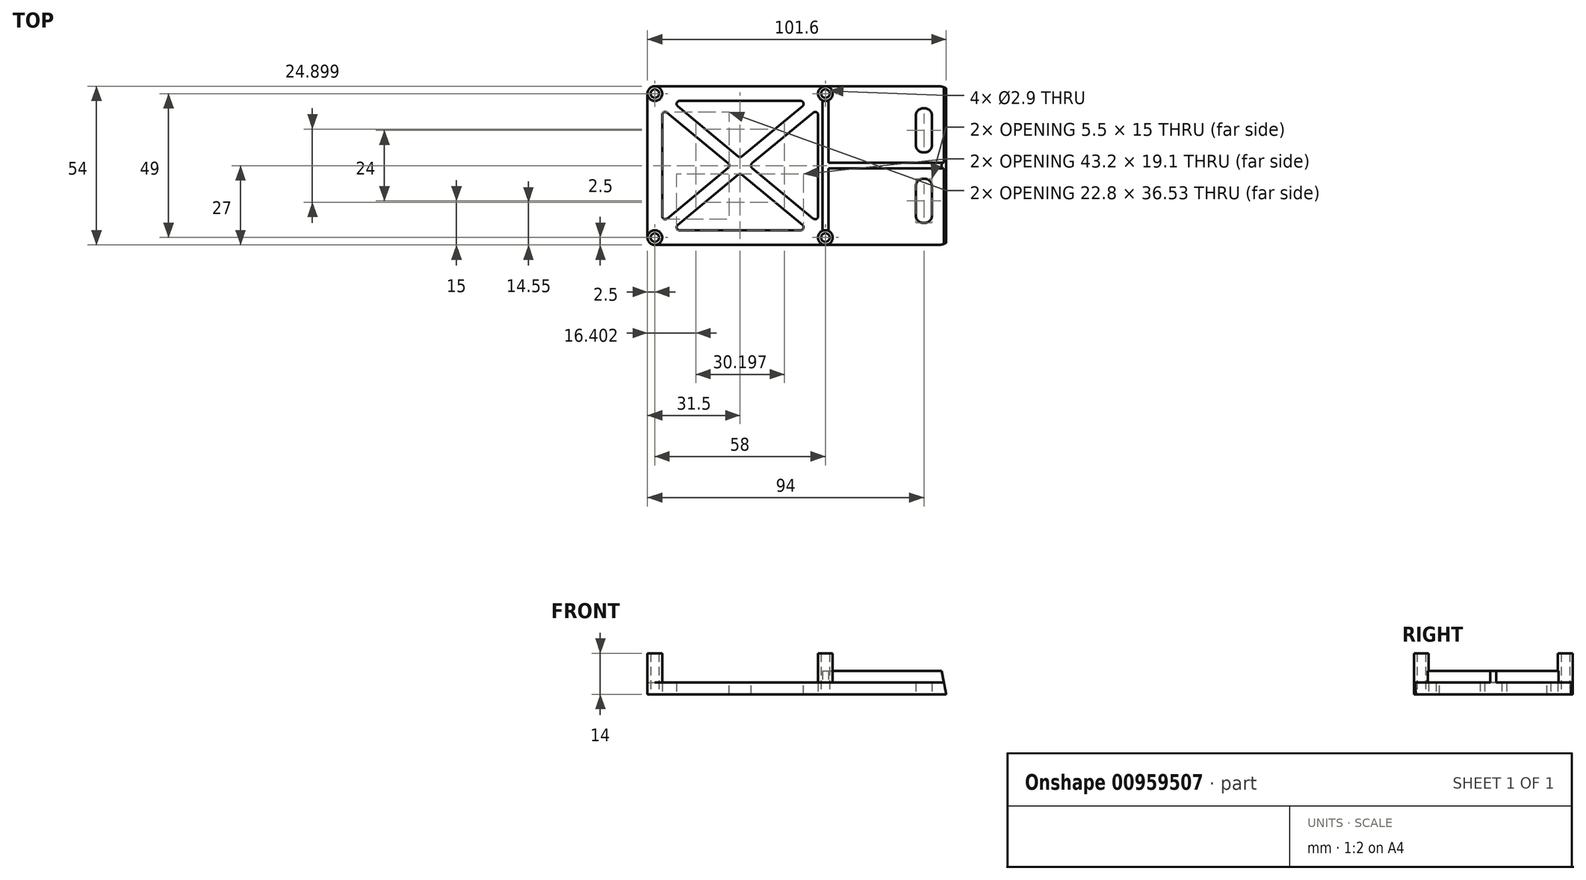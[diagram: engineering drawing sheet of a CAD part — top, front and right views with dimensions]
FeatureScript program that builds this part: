
annotation { "Feature Type Name" : "Feature", "Feature Type Description" : "" }
export const myFeature = defineFeature(function(context is Context, id is Id, definition is map)
    precondition{}
    {
        {
            var Q0;
            Q0=qCreatedBy(makeId("Top.planeOp"),FACE);
            var sketch = newSketch(context, id + "F0", { "sketchPlane" : qUnion([Q0])});
            skLineSegment(sketch, "E0.bottom", {"start": v(37.5, -28) * mm, "end": v(-47.5, -28) * mm, "construction": true});
            skLineSegment(sketch, "E0.top", {"start": v(37.5, 28) * mm, "end": v(-47.5, 28) * mm, "construction": true});
            skLineSegment(sketch, "E0.left", {"start": v(37.5, -28) * mm, "end": v(37.5, 28) * mm, "construction": true});
            skLineSegment(sketch, "E0.right", {"start": v(-47.5, -28) * mm, "end": v(-47.5, 28) * mm, "construction": true});
            skLineSegment(sketch, "E1.bottom", {"start": v(-44, -24.5) * mm, "end": v(14, -24.5) * mm, "construction": true});
            skLineSegment(sketch, "E1.top", {"start": v(-44, 24.5) * mm, "end": v(14, 24.5) * mm, "construction": true});
            skLineSegment(sketch, "E1.left", {"start": v(-44, -24.5) * mm, "end": v(-44, 24.5) * mm, "construction": true});
            skLineSegment(sketch, "E1.right", {"start": v(14, -24.5) * mm, "end": v(14, 24.5) * mm, "construction": true});
            skSolve(sketch);
        }
        {
            var Q0;
            Q0=qCreatedBy(makeId("Top.planeOp"),FACE);
            var sketch = newSketch(context, id + "F1", { "sketchPlane" : qUnion([Q0])});
            skPoint(sketch, "E2.0", {"position": v(-44, 24.5) * mm});
            skPoint(sketch, "E3.0", {"position": v(14, 24.5) * mm});
            skPoint(sketch, "E4.0", {"position": v(14, -24.5) * mm});
            skPoint(sketch, "E5.0", {"position": v(-44, -24.5) * mm});
            skCircle(sketch, "E6", {"center": v(-44, 24.5) * mm, "radius": 2.5 * mm});
            skCircle(sketch, "E7", {"center": v(14, 24.5) * mm, "radius": 2.5 * mm});
            skCircle(sketch, "E8", {"center": v(14, -24.5) * mm, "radius": 2.5 * mm});
            skCircle(sketch, "E9", {"center": v(-44, -24.5) * mm, "radius": 2.5 * mm});
            skCircle(sketch, "E10", {"center": v(-44, 24.5) * mm, "radius": 1.45 * mm});
            skCircle(sketch, "E11", {"center": v(14, 24.5) * mm, "radius": 1.45 * mm});
            skCircle(sketch, "E12", {"center": v(14, -24.5) * mm, "radius": 1.45 * mm});
            skCircle(sketch, "E13", {"center": v(-44, -24.5) * mm, "radius": 1.45 * mm});
            skPoint(sketch, "E14.0", {"position": v(-15, 24.5) * mm});
            skPoint(sketch, "E15.0", {"position": v(-44, 0) * mm});
            skLineSegment(sketch, "E16.bottom", {"start": v(16.5, -27) * mm, "end": v(-46.5, -27) * mm});
            skLineSegment(sketch, "E16.top", {"start": v(16.5, 27) * mm, "end": v(-46.5, 27) * mm});
            skLineSegment(sketch, "E16.left", {"start": v(16.5, -27) * mm, "end": v(16.5, 27) * mm, "construction": true});
            skLineSegment(sketch, "E16.right", {"start": v(-46.5, -27) * mm, "end": v(-46.5, 27) * mm});
            skPoint(sketch, "E16.middle", {"position": v(-15, 0) * mm});
            skLineSegment(sketch, "E17", {"start": v(16.5, -27) * mm, "end": v(57.5, -27) * mm});
            skLineSegment(sketch, "E18", {"start": v(57.5, -27) * mm, "end": v(57.5, 27) * mm});
            skLineSegment(sketch, "E19", {"start": v(57.5, 27) * mm, "end": v(16.5, 27) * mm});
            skLineSegment(sketch, "E20", {"start": v(47.5, 27) * mm, "end": v(47.5, -27) * mm, "construction": true});
            skLineSegment(sketch, "E21.bottom", {"start": v(11.5, -22) * mm, "end": v(-41.5, -22) * mm});
            skLineSegment(sketch, "E21.top", {"start": v(11.5, 22) * mm, "end": v(-41.5, 22) * mm});
            skLineSegment(sketch, "E21.left", {"start": v(11.5, -22) * mm, "end": v(11.5, 22) * mm});
            skLineSegment(sketch, "E21.right", {"start": v(-41.5, -22) * mm, "end": v(-41.5, 22) * mm});
            skLineSegment(sketch, "E22.bottom", {"start": v(50.25, 4.5) * mm, "end": v(44.75, 4.5) * mm});
            skLineSegment(sketch, "E22.top", {"start": v(50.25, 19.5) * mm, "end": v(44.75, 19.5) * mm});
            skLineSegment(sketch, "E22.left", {"start": v(50.25, 4.5) * mm, "end": v(50.25, 19.5) * mm});
            skLineSegment(sketch, "E22.right", {"start": v(44.75, 4.5) * mm, "end": v(44.75, 19.5) * mm});
            skPoint(sketch, "E22.middle", {"position": v(47.5, 12) * mm});
            skLineSegment(sketch, "E23.bottom", {"start": v(44.75, -19.5) * mm, "end": v(50.25, -19.5) * mm});
            skLineSegment(sketch, "E23.top", {"start": v(44.75, -4.5) * mm, "end": v(50.25, -4.5) * mm});
            skLineSegment(sketch, "E23.left", {"start": v(44.75, -19.5) * mm, "end": v(44.75, -4.5) * mm});
            skLineSegment(sketch, "E23.right", {"start": v(50.25, -19.5) * mm, "end": v(50.25, -4.5) * mm});
            skPoint(sketch, "E23.middle", {"position": v(47.5, -12) * mm});
            skPoint(sketch, "E24.0", {"position": v(37.5, 0) * mm});
            skLineSegment(sketch, "E25", {"start": v(11.5, 22) * mm, "end": v(-41.5, -22) * mm, "construction": true});
            skLineSegment(sketch, "E26", {"start": v(-41.5, 22) * mm, "end": v(11.5, -22) * mm, "construction": true});
            skArc(sketch, "E27.0.startCap", {"start": v(-42.78, 20.46) * mm, "mid": v(-43.04, 23.28) * mm, "end": v(-40.22, 23.54) * mm, "construction": true});
            skArc(sketch, "E27.0.endCap", {"start": v(12.78, -20.46) * mm, "mid": v(13.04, -23.28) * mm, "end": v(10.22, -23.54) * mm, "construction": true});
            skLineSegment(sketch, "E27.0.left", {"start": v(-40.22, 23.54) * mm, "end": v(12.78, -20.46) * mm});
            skLineSegment(sketch, "E27.0.right", {"start": v(-42.78, 20.46) * mm, "end": v(10.22, -23.54) * mm});
            skArc(sketch, "E27.1.startCap", {"start": v(10.22, 23.54) * mm, "mid": v(13.04, 23.28) * mm, "end": v(12.78, 20.46) * mm, "construction": true});
            skArc(sketch, "E27.1.endCap", {"start": v(-40.22, -23.54) * mm, "mid": v(-43.04, -23.28) * mm, "end": v(-42.78, -20.46) * mm, "construction": true});
            skLineSegment(sketch, "E27.1.left", {"start": v(12.78, 20.46) * mm, "end": v(-40.22, -23.54) * mm});
            skLineSegment(sketch, "E27.1.right", {"start": v(10.22, 23.54) * mm, "end": v(-42.78, -20.46) * mm});
            skSolve(sketch);
        }
        {
            var Q0;
            Q0=makeQuery(id+"F1.imprint","IMPRINT",FACE,{"disambiguationData":[TD([[makeQuery(id+"F1.imprint","IMPRINT",EDGE,{"derivedFrom":sQuery(id+"F1.wireOp",EDGE,"E7")}),1.0]])]});
            var Q1;
            Q1=makeQuery(id+"F1.imprint","IMPRINT",FACE,{"disambiguationData":[TD([[makeQuery(id+"F1.imprint","IMPRINT",EDGE,{"derivedFrom":sQuery(id+"F1.wireOp",EDGE,"E8")}),1.0]])]});
            var Q2;
            Q2=makeQuery(id+"F1.imprint","IMPRINT",FACE,{"disambiguationData":[TD([[makeQuery(id+"F1.imprint","IMPRINT",EDGE,{"derivedFrom":sQuery(id+"F1.wireOp",EDGE,"E10")}),-1.0]])]});
            var Q3;
            Q3=makeQuery(id+"F1.imprint","IMPRINT",FACE,{"disambiguationData":[TD([[makeQuery(id+"F1.imprint","IMPRINT",EDGE,{"derivedFrom":sQuery(id+"F1.wireOp",EDGE,"E13")}),-1.0]])]});
            var Q4;
            {var subQ13=sQuery(id+"F1.wireOp",EDGE,"E7");Q4=makeQuery(id+"F1.imprint","IMPRINT",FACE,{"disambiguationData":[TD([[makeQuery(id+"F1.imprint","IMPRINT",EDGE,{"derivedFrom":subQ13}),-1.0]])]});}
            var Q5;
            {var subQ1=sQuery(id+"F1.wireOp",EDGE,"E21.right");var subQ5=sQuery(id+"F1.wireOp",EDGE,"E21.top");var subQ6=makeQuery(id+"F1.imprint","INTERSECT",VERTEX,{"derivedFrom":[subQ5,subQ1]});Q5=makeQuery(id+"F1.imprint","IMPRINT",FACE,{"disambiguationData":[TD([[makeQuery(id+"F1.imprint","IMPRINT",EDGE,{"disambiguationData":[TD([[subQ6,1.0]])],"derivedFrom":subQ5}),1.0]])]});}
            var Q6;
            {var subQ1=sQuery(id+"F1.wireOp",EDGE,"E21.left");var subQ7=sQuery(id+"F1.wireOp",EDGE,"E21.top");var subQ8=makeQuery(id+"F1.imprint","INTERSECT",VERTEX,{"derivedFrom":[subQ7,subQ1]});Q6=makeQuery(id+"F1.imprint","IMPRINT",FACE,{"disambiguationData":[TD([[makeQuery(id+"F1.imprint","IMPRINT",EDGE,{"disambiguationData":[TD([[subQ8,-1.0]])],"derivedFrom":subQ7}),1.0]])]});}
            var Q7;
            {var subQ0=sQuery(id+"F1.wireOp",EDGE,"E27.1.right");var subQ1=sQuery(id+"F1.wireOp",EDGE,"E27.0.left");var subQ2=makeQuery(id+"F1.imprint","INTERSECT",VERTEX,{"derivedFrom":[subQ1,subQ0]});Q7=makeQuery(id+"F1.imprint","IMPRINT",FACE,{"disambiguationData":[TD([[makeQuery(id+"F1.imprint","IMPRINT",EDGE,{"disambiguationData":[TD([[subQ2,-1.0]])],"derivedFrom":subQ1}),-1.0]])]});}
            var Q8;
            {var subQ1=sQuery(id+"F1.wireOp",EDGE,"E21.left");var subQ5=sQuery(id+"F1.wireOp",EDGE,"E21.bottom");var subQ6=makeQuery(id+"F1.imprint","INTERSECT",VERTEX,{"derivedFrom":[subQ5,subQ1]});Q8=makeQuery(id+"F1.imprint","IMPRINT",FACE,{"disambiguationData":[TD([[makeQuery(id+"F1.imprint","IMPRINT",EDGE,{"disambiguationData":[TD([[subQ6,-1.0]])],"derivedFrom":subQ5}),-1.0]])]});}
            var Q9;
            {var subQ1=sQuery(id+"F1.wireOp",EDGE,"E21.bottom");var subQ7=sQuery(id+"F1.wireOp",EDGE,"E21.right");var subQ8=makeQuery(id+"F1.imprint","INTERSECT",VERTEX,{"derivedFrom":[subQ1,subQ7]});Q9=makeQuery(id+"F1.imprint","IMPRINT",FACE,{"disambiguationData":[TD([[makeQuery(id+"F1.imprint","IMPRINT",EDGE,{"disambiguationData":[TD([[subQ8,1.0]])],"derivedFrom":subQ1}),-1.0]])]});}
            var Q10;
            Q10 = qConstructionFilter(qBodyType(qCreatedBy(id + "F1" ,EDGE), BodyType.WIRE), ConstructionObject.NO);
            extrude(context, id + "F2", {"entities" : qUnion([Q0, Q1, Q2, Q3, Q4, Q5, Q6, Q7, Q8, Q9]), "surfaceEntities" : qUnion([Q10]), "depth" : 4 * mm, "offsetDistance" : 25 * mm});
        }
        {
            var Q0;
            Q0=makeQuery(id+"F1.imprint","IMPRINT",FACE,{"disambiguationData":[TD([[makeQuery(id+"F1.imprint","IMPRINT",EDGE,{"derivedFrom":sQuery(id+"F1.wireOp",EDGE,"E10")}),-1.0]])]});
            var Q1;
            Q1=makeQuery(id+"F1.imprint","IMPRINT",FACE,{"disambiguationData":[TD([[makeQuery(id+"F1.imprint","IMPRINT",EDGE,{"derivedFrom":sQuery(id+"F1.wireOp",EDGE,"E7")}),1.0]])]});
            var Q2;
            Q2=makeQuery(id+"F1.imprint","IMPRINT",FACE,{"disambiguationData":[TD([[makeQuery(id+"F1.imprint","IMPRINT",EDGE,{"derivedFrom":sQuery(id+"F1.wireOp",EDGE,"E8")}),1.0]])]});
            var Q3;
            Q3=makeQuery(id+"F1.imprint","IMPRINT",FACE,{"disambiguationData":[TD([[makeQuery(id+"F1.imprint","IMPRINT",EDGE,{"derivedFrom":sQuery(id+"F1.wireOp",EDGE,"E13")}),-1.0]])]});
            extrude(context, id + "F3", {"entities" : qUnion([Q0, Q1, Q2, Q3]), "operationType" : NewBodyOperationType.ADD, "depth" : 14 * mm, "offsetDistance" : 25 * mm});
        }
        {
            var Q0;
            Q0=makeQuery(id+"F2.opExtrude","SWEPT_EDGE",EDGE,{"disambiguationData":[OSD([sQuery(id+"F1.wireOp",EDGE,"E22.top"),sQuery(id+"F1.wireOp",EDGE,"E22.right")])]});
            var Q1;
            Q1=makeQuery(id+"F2.opExtrude","SWEPT_EDGE",EDGE,{"disambiguationData":[OSD([sQuery(id+"F1.wireOp",EDGE,"E22.top"),sQuery(id+"F1.wireOp",EDGE,"E22.left")])]});
            var Q2;
            Q2=makeQuery(id+"F2.opExtrude","SWEPT_EDGE",EDGE,{"disambiguationData":[OSD([sQuery(id+"F1.wireOp",EDGE,"E22.bottom"),sQuery(id+"F1.wireOp",EDGE,"E22.left")])]});
            var Q3;
            Q3=makeQuery(id+"F2.opExtrude","SWEPT_EDGE",EDGE,{"disambiguationData":[OSD([sQuery(id+"F1.wireOp",EDGE,"E22.bottom"),sQuery(id+"F1.wireOp",EDGE,"E22.right")])]});
            var Q4;
            Q4=makeQuery(id+"F2.opExtrude","SWEPT_EDGE",EDGE,{"disambiguationData":[OSD([sQuery(id+"F1.wireOp",EDGE,"E23.bottom"),sQuery(id+"F1.wireOp",EDGE,"E23.left")])]});
            var Q5;
            Q5=makeQuery(id+"F2.opExtrude","SWEPT_EDGE",EDGE,{"disambiguationData":[OSD([sQuery(id+"F1.wireOp",EDGE,"E23.bottom"),sQuery(id+"F1.wireOp",EDGE,"E23.right")])]});
            var Q6;
            Q6=makeQuery(id+"F2.opExtrude","SWEPT_EDGE",EDGE,{"disambiguationData":[OSD([sQuery(id+"F1.wireOp",EDGE,"E23.top"),sQuery(id+"F1.wireOp",EDGE,"E23.right")])]});
            var Q7;
            Q7=makeQuery(id+"F2.opExtrude","SWEPT_EDGE",EDGE,{"disambiguationData":[OSD([sQuery(id+"F1.wireOp",EDGE,"E23.top"),sQuery(id+"F1.wireOp",EDGE,"E23.left")])]});
            fillet(context, id + "F4", {"entities" : qUnion([Q0, Q1, Q2, Q3, Q4, Q5, Q6, Q7]), "radius" : 2.5 * mm, "tangentPropagation" : true, "allowEdgeOverflow" : false});
        }
        {
            var Q0;
            Q0=makeQuery(id+"F2.opExtrude","SWEPT_EDGE",EDGE,{"disambiguationData":[OSD([sQuery(id+"F1.wireOp",EDGE,"E17"),sQuery(id+"F1.wireOp",EDGE,"E18")])]});
            var Q1;
            Q1=makeQuery(id+"F2.opExtrude","SWEPT_EDGE",EDGE,{"disambiguationData":[OSD([sQuery(id+"F1.wireOp",EDGE,"E18"),sQuery(id+"F1.wireOp",EDGE,"E19")])]});
            fillet(context, id + "F5", {"entities" : qUnion([Q0, Q1]), "radius" : 5 * mm, "tangentPropagation" : true, "allowEdgeOverflow" : false});
        }
        {
            var Q0;
            Q0=makeQuery(id+"F2.opExtrude","CAP_FACE",FACE,{"disambiguationData":[OSD([sQuery(id+"F1.wireOp",EDGE,"E6"),sQuery(id+"F1.wireOp",EDGE,"E9"),sQuery(id+"F1.wireOp",EDGE,"E10"),sQuery(id+"F1.wireOp",EDGE,"E11"),sQuery(id+"F1.wireOp",EDGE,"E12"),sQuery(id+"F1.wireOp",EDGE,"E13"),sQuery(id+"F1.wireOp",EDGE,"E16.bottom"),sQuery(id+"F1.wireOp",EDGE,"E16.top"),sQuery(id+"F1.wireOp",EDGE,"E16.right"),sQuery(id+"F1.wireOp",EDGE,"E17"),sQuery(id+"F1.wireOp",EDGE,"E18"),sQuery(id+"F1.wireOp",EDGE,"E19"),sQuery(id+"F1.wireOp",EDGE,"E21.bottom"),sQuery(id+"F1.wireOp",EDGE,"E21.top"),sQuery(id+"F1.wireOp",EDGE,"E21.left"),sQuery(id+"F1.wireOp",EDGE,"E21.right"),sQuery(id+"F1.wireOp",EDGE,"E22.bottom"),sQuery(id+"F1.wireOp",EDGE,"E22.top"),sQuery(id+"F1.wireOp",EDGE,"E22.left"),sQuery(id+"F1.wireOp",EDGE,"E22.right"),sQuery(id+"F1.wireOp",EDGE,"E23.bottom"),sQuery(id+"F1.wireOp",EDGE,"E23.top"),sQuery(id+"F1.wireOp",EDGE,"E23.left"),sQuery(id+"F1.wireOp",EDGE,"E23.right"),sQuery(id+"F1.wireOp",EDGE,"E27.0.left"),sQuery(id+"F1.wireOp",EDGE,"E27.0.right"),sQuery(id+"F1.wireOp",EDGE,"E27.1.left"),sQuery(id+"F1.wireOp",EDGE,"E27.1.right")])],"isStart":false});
            var sketch = newSketch(context, id + "F6", { "sketchPlane" : qUnion([Q0])});
            skLineSegment(sketch, "E28", {"start": v(13, 22.2) * mm, "end": v(13, -22.2) * mm});
            skLineSegment(sketch, "E29", {"start": v(15, 22.2) * mm, "end": v(15, -22.2) * mm});
            skLineSegment(sketch, "E30", {"start": v(15, -1) * mm, "end": v(57.5, -1) * mm});
            skLineSegment(sketch, "E31", {"start": v(15, 1) * mm, "end": v(57.5, 1) * mm});
            skSolve(sketch);
        }
        {
            var Q0;
            {var subQ8=sQuery(id+"F6.wireOp",EDGE,"E28");Q0=makeQuery(id+"F6.imprint","IMPRINT",FACE,{"disambiguationData":[TD([[makeQuery(id+"F6.imprint","IMPRINT",EDGE,{"derivedFrom":subQ8}),1.0]])]});}
            var Q1;
            {var subQ0=sQuery(id+"F6.wireOp",EDGE,"E30");Q1=makeQuery(id+"F6.imprint","IMPRINT",FACE,{"disambiguationData":[TD([[makeQuery(id+"F6.imprint","IMPRINT",EDGE,{"derivedFrom":subQ0}),1.0]])]});}
            extrude(context, id + "F7", {"entities" : qUnion([Q0, Q1]), "operationType" : NewBodyOperationType.ADD, "depth" : 4 * mm, "offsetDistance" : 25 * mm});
        }
        {
            var Q0;
            Q0=makeQuery(id+"F7.opExtrude","CAP_EDGE",EDGE,{"disambiguationData":[OSD([sQuery(id+"F1.wireOp",EDGE,"E18")])],"isStart":false});
            chamfer(context, id + "F8", {"entities" : qUnion([Q0]), "chamferType" : ChamferType.TWO_OFFSETS, "width1" : 20 * mm, "oppositeDirection" : false, "width2" : 4 * mm, "tangentPropagation" : true});
        }
        {
            var Q0;
            Q0=makeQuery(id+"F2.opExtrude","SWEPT_EDGE",EDGE,{"disambiguationData":[OSD([sQuery(id+"F1.wireOp",EDGE,"E21.right"),sQuery(id+"F1.wireOp",EDGE,"E27.0.right")])]});
            var Q1;
            Q1=makeQuery(id+"F2.opExtrude","SWEPT_EDGE",EDGE,{"disambiguationData":[OSD([sQuery(id+"F1.wireOp",EDGE,"E21.top"),sQuery(id+"F1.wireOp",EDGE,"E27.0.left")])]});
            var Q2;
            Q2=makeQuery(id+"F2.opExtrude","SWEPT_EDGE",EDGE,{"disambiguationData":[OSD([sQuery(id+"F1.wireOp",EDGE,"E21.top"),sQuery(id+"F1.wireOp",EDGE,"E27.1.right")])]});
            var Q3;
            Q3=makeQuery(id+"F2.opExtrude","SWEPT_EDGE",EDGE,{"disambiguationData":[OSD([sQuery(id+"F1.wireOp",EDGE,"E21.left"),sQuery(id+"F1.wireOp",EDGE,"E27.1.left")])]});
            var Q4;
            Q4=makeQuery(id+"F2.opExtrude","SWEPT_EDGE",EDGE,{"disambiguationData":[OSD([sQuery(id+"F1.wireOp",EDGE,"E21.left"),sQuery(id+"F1.wireOp",EDGE,"E27.0.left")])]});
            var Q5;
            Q5=makeQuery(id+"F2.opExtrude","SWEPT_EDGE",EDGE,{"disambiguationData":[OSD([sQuery(id+"F1.wireOp",EDGE,"E21.bottom"),sQuery(id+"F1.wireOp",EDGE,"E27.0.right")])]});
            var Q6;
            Q6=makeQuery(id+"F2.opExtrude","SWEPT_EDGE",EDGE,{"disambiguationData":[OSD([sQuery(id+"F1.wireOp",EDGE,"E21.bottom"),sQuery(id+"F1.wireOp",EDGE,"E27.1.left")])]});
            var Q7;
            Q7=makeQuery(id+"F2.opExtrude","SWEPT_EDGE",EDGE,{"disambiguationData":[OSD([sQuery(id+"F1.wireOp",EDGE,"E21.right"),sQuery(id+"F1.wireOp",EDGE,"E27.1.right")])]});
            var Q8;
            Q8=makeQuery(id+"F2.opExtrude","SWEPT_EDGE",EDGE,{"disambiguationData":[OSD([sQuery(id+"F1.wireOp",EDGE,"E27.0.right"),sQuery(id+"F1.wireOp",EDGE,"E27.1.right")])]});
            var Q9;
            Q9=makeQuery(id+"F2.opExtrude","SWEPT_EDGE",EDGE,{"disambiguationData":[OSD([sQuery(id+"F1.wireOp",EDGE,"E27.0.right"),sQuery(id+"F1.wireOp",EDGE,"E27.1.left")])]});
            var Q10;
            Q10=makeQuery(id+"F2.opExtrude","SWEPT_EDGE",EDGE,{"disambiguationData":[OSD([sQuery(id+"F1.wireOp",EDGE,"E27.0.left"),sQuery(id+"F1.wireOp",EDGE,"E27.1.left")])]});
            var Q11;
            Q11=makeQuery(id+"F2.opExtrude","SWEPT_EDGE",EDGE,{"disambiguationData":[OSD([sQuery(id+"F1.wireOp",EDGE,"E27.0.left"),sQuery(id+"F1.wireOp",EDGE,"E27.1.right")])]});
            fillet(context, id + "F9", {"entities" : qUnion([Q0, Q1, Q2, Q3, Q4, Q5, Q6, Q7, Q8, Q9, Q10, Q11]), "radius" : 1 * mm, "tangentPropagation" : true, "allowEdgeOverflow" : false});
        }
    });
